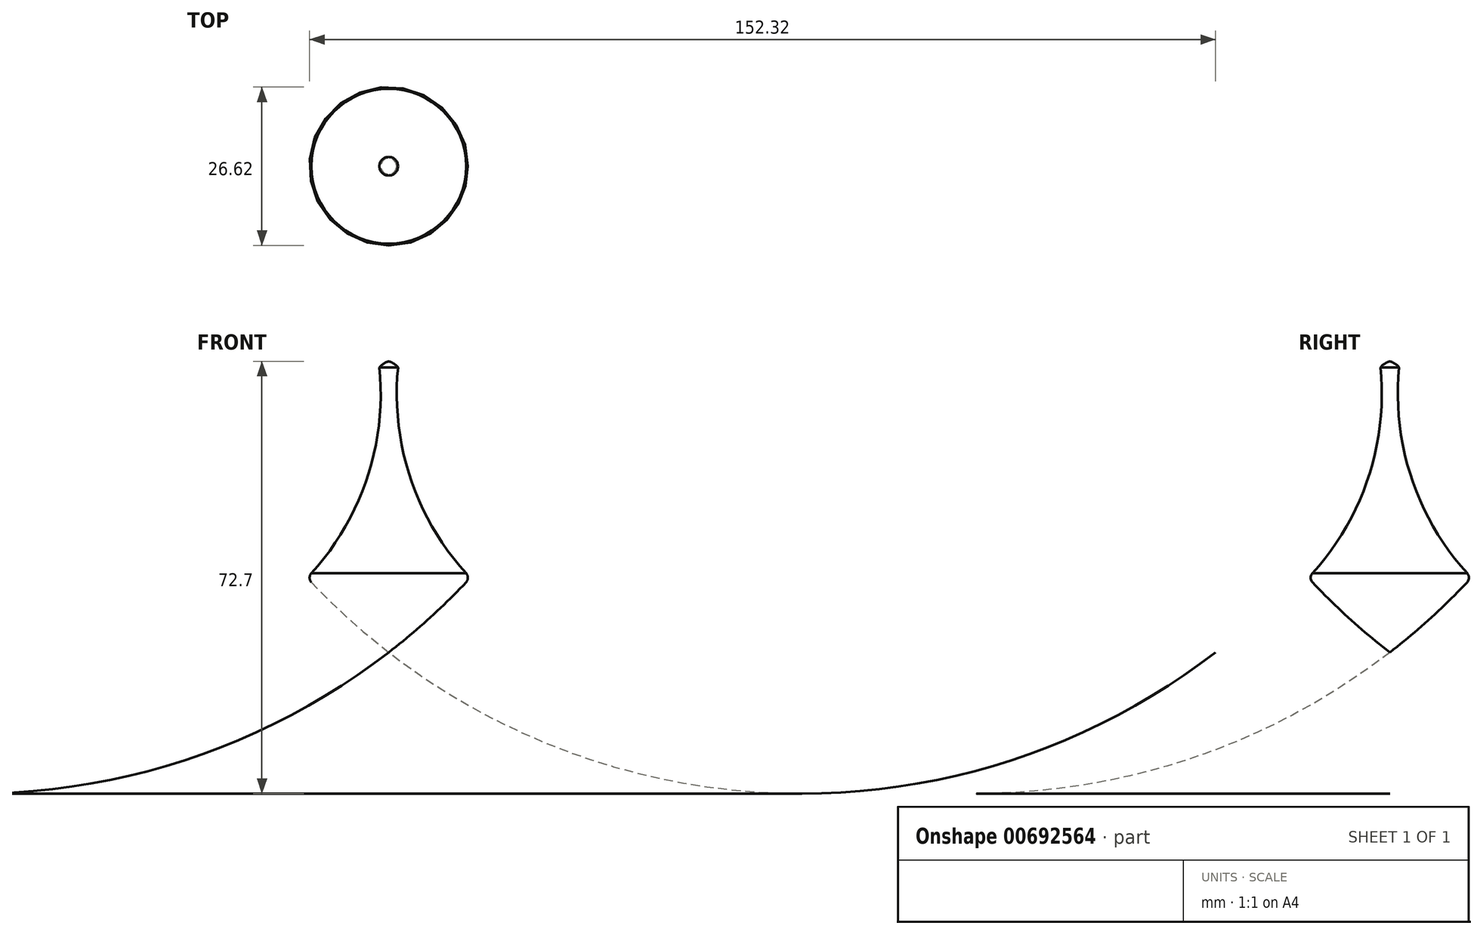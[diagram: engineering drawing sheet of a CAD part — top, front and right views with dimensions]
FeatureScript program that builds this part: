
annotation { "Feature Type Name" : "Feature", "Feature Type Description" : "" }
export const myFeature = defineFeature(function(context is Context, id is Id, definition is map)
    precondition{}
    {
        {
            var Q0;
            Q0=qCreatedBy(makeId("Front.planeOp"),FACE);
            var sketch = newSketch(context, id + "F0", { "sketchPlane" : qUnion([Q0])});
            skArc(sketch, "E0", {"start": v(1.56, 47.94) * mm, "mid": v(3.62, 29.4) * mm, "end": v(13.01, 13.28) * mm});
            skArc(sketch, "E1", {"start": v(1.56, 47.94) * mm, "mid": v(0.86, 48.56) * mm, "end": v(0, 48.95) * mm});
            skLineSegment(sketch, "E2", {"start": v(0, -1.02) * mm, "end": v(0, 48.95) * mm});
            skLineSegment(sketch, "E3", {"start": v(0, 53.77) * mm, "end": v(0, -8.35) * mm, "construction": true});
            skArc(sketch, "E4", {"start": v(13.01, 11.78) * mm, "mid": v(13.31, 12.53) * mm, "end": v(13.01, 13.28) * mm});
            skArc(sketch, "E5", {"start": v(0, 0) * mm, "mid": v(6.73, 5.64) * mm, "end": v(13.01, 11.78) * mm});
            skSolve(sketch);
        }
        {
            var Q0;
            Q0 = qSketchRegion(id + "F0", true);
            var Q1;
            Q1=sQuery(id+"F0.wireOp",EDGE,"E3");
            revolve(context, id + "F1", {"entities" : qUnion([Q0]), "axis" : qUnion([Q1]), "revolveType" : RevolveType.FULL});
        }
    });
